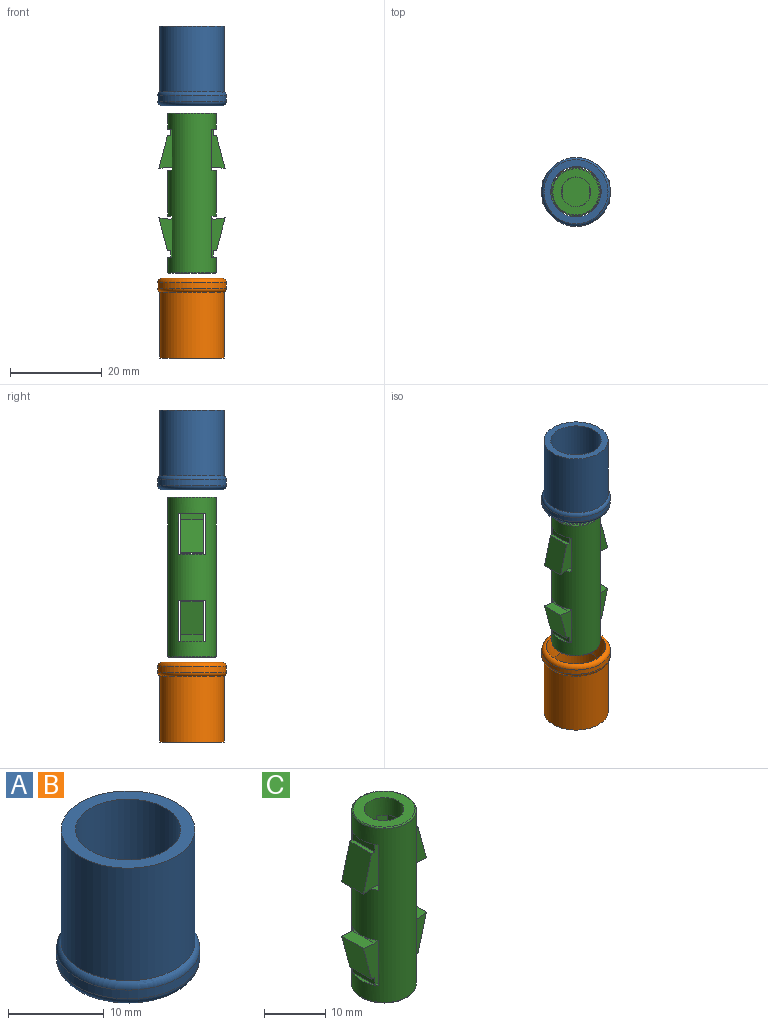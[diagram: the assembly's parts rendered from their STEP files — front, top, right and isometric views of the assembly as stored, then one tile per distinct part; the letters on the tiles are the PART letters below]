
ASSEMBLY  parts=3 mates=2
PART A: 7 faces, bbox 16.2x16.2x17.4 mm
  f0: cylinder r=7mm len=14.4mm, axis (0,0,-1), area 633.3mm2, adj f2,f5
  f1: cylinder r=5.5mm len=12.4mm, axis (0,0,-1), area 428.5mm2, adj f2,f6
  f2: plane 14x14mm, normal (0,0,1), area 58.9mm2, adj f0,f1
  f3: cylinder r=7.5mm len=15mm, axis (0,0,-1), area 53.4mm2, adj f4,f5
  f4: torus R=6.5mm, axis (0,0,1), area 70.4mm2, adj f3,f6
  f5: torus R=6.5mm, axis (0,0,1), area 48.2mm2, adj f0,f3
  f6: cone r=6.5mm half-angle=11.3deg, axis (0,0,-1), area 192.2mm2, adj f1,f4
PART B: same geometry as A
PART C: 89 faces, bbox 14.5x11.4x35 mm
  f0: cylinder r=3.25mm len=17mm, axis (0,0,-1), area 209.6mm2, adj f1,f2,f4,f12,f13,f14,f15,f17
  f1: plane 3.37x3mm, normal (0,0,1), area 2.3mm2, adj f0,f10,f13,f77,f83
  f2: plane 3.37x3mm, normal (0,0,1), area 2.3mm2, adj f0,f10,f15,f77,f84
  f3: plane 4.87x0.6mm, normal (0,0,1), area 2mm2, adj f10,f66
  f4: plane 3.37x3mm, normal (0,0,1), area 2.3mm2, adj f0,f10,f18,f64,f70
  f5: plane 4.87x0.6mm, normal (0,0,-1), area 2mm2, adj f10,f52
  f6: plane 3.37x3mm, normal (0,0,-1), area 2.3mm2, adj f9,f10,f26,f51,f55
  f7: plane 3.37x3mm, normal (0,0,-1), area 2.3mm2, adj f9,f10,f21,f35,f42
  f8: plane 4.87x0.6mm, normal (0,0,-1), area 2mm2, adj f10,f33
  f9: cylinder r=3.25mm len=17mm, axis (0,0,-1), area 209.6mm2, adj f6,f7,f11,f21,f22,f23,f24,f25
  f10: cylinder r=5.25mm len=34.6mm, axis (0,0,-1), area 911.4mm2, adj f1,f2,f3,f4,f5,f6,f7,f8
  f11: plane 10.1x10.1mm, normal (0,0,1), area 46.9mm2, adj f9,f88
  f12: plane 10.1x10.1mm, normal (0,0,-1), area 46.9mm2, adj f0,f87
  f13: plane 9x3.06mm, normal (0,1,0), area 27.5mm2, adj f0,f1,f10,f14
  f14: plane 6x4mm, normal (0,0,-1), area 13.5mm2, adj f0,f10,f13,f15
  f15: plane 9x3.06mm, normal (0,-1,0), area 27.5mm2, adj f0,f2,f10,f14
  f16: plane 4.87x0.6mm, normal (0,0,1), area 2mm2, adj f10,f76
  f17: plane 3.37x3mm, normal (0,0,1), area 2.3mm2, adj f0,f10,f20,f64,f69
  f18: plane 9x3.06mm, normal (0,-1,0), area 27.5mm2, adj f0,f4,f10,f19
  f19: plane 6x4mm, normal (0,0,-1), area 13.5mm2, adj f0,f10,f18,f20
  f20: plane 9x3.06mm, normal (0,1,0), area 27.5mm2, adj f0,f10,f17,f19
  f21: plane 9x3.06mm, normal (0,-1,0), area 27.5mm2, adj f7,f9,f10,f22
  f22: plane 6x4mm, normal (0,0,1), area 13.5mm2, adj f9,f10,f21,f23
  f23: plane 9x3.06mm, normal (0,1,0), area 27.5mm2, adj f9,f10,f22,f24
  f24: plane 3.37x3mm, normal (0,0,-1), area 2.3mm2, adj f9,f10,f23,f35,f41
  f25: plane 3.37x3mm, normal (0,0,-1), area 2.3mm2, adj f9,f10,f28,f51,f56
  f26: plane 9x3.06mm, normal (0,1,0), area 27.5mm2, adj f6,f9,f10,f27
  f27: plane 6x4mm, normal (0,0,1), area 13.5mm2, adj f9,f10,f26,f28
  f28: plane 9x3.06mm, normal (0,-1,0), area 27.5mm2, adj f9,f10,f25,f27
  f29: plane 0.06x0.03mm, normal (0,0,1), area 0mm2, adj f10,f33,f42
  f30: plane 5x2.58mm, normal (-0.12,0,-0.99), area 13mm2, adj f31,f40,f41,f42
  f31: plane 7.1x5mm, normal (0.97,0,0.26), area 36.7mm2, adj f30,f32,f41,f42
  f32: plane 5x0.7mm, normal (0,0,1), area 3.5mm2, adj f31,f33,f41,f42
  f33: plane 5x1.5mm, normal (1,0,0), area 7.5mm2, adj f8,f29,f32,f34,f41,f42
  f34: plane 0.06x0.03mm, normal (0,0,1), area 0mm2, adj f10,f33,f41
  f35: plane 7.8x5mm, normal (-1,0,0), area 39mm2, adj f7,f24,f36,f41,f42
  f36: plane 5x0.25mm, normal (0,0,1), area 1.2mm2, adj f35,f37,f41,f42
  f37: plane 5x0.5mm, normal (-1,0,0), area 2.5mm2, adj f36,f38,f41,f42
  f38: plane 5x0.25mm, normal (0,0,-1), area 1.2mm2, adj f37,f39,f41,f42
  f39: plane 5x0.5mm, normal (-1,0,0), area 2.5mm2, adj f38,f40,f41,f42
  f40: plane 5x1.41mm, normal (0.34,0,-0.94), area 7.5mm2, adj f30,f39,f41,f42
  f41: plane 8.8x4.25mm, normal (0,-1,0), area 23.4mm2, adj f24,f30,f31,f32,f33,f34,f35,f36
  f42: plane 8.8x4.25mm, normal (0,1,0), area 23.4mm2, adj f7,f29,f30,f31,f32,f33,f35,f36
  f43: plane 0.06x0.03mm, normal (0,0,1), area 0mm2, adj f10,f52,f55
  f44: plane 0.06x0.03mm, normal (0,0,1), area 0mm2, adj f10,f52,f56
  f45: plane 5x2.58mm, normal (0.12,0,-0.99), area 13mm2, adj f46,f54,f55,f56
  f46: plane 5x1.41mm, normal (-0.34,0,-0.94), area 7.5mm2, adj f45,f47,f55,f56
  f47: plane 5x0.5mm, normal (1,0,0), area 2.5mm2, adj f46,f48,f55,f56
  f48: plane 5x0.25mm, normal (0,0,-1), area 1.2mm2, adj f47,f49,f55,f56
  f49: plane 5x0.5mm, normal (1,0,0), area 2.5mm2, adj f48,f50,f55,f56
  f50: plane 5x0.25mm, normal (0,0,1), area 1.2mm2, adj f49,f51,f55,f56
  f51: plane 7.8x5mm, normal (1,0,0), area 39mm2, adj f6,f25,f50,f55,f56
  f52: plane 5x1.5mm, normal (-1,0,0), area 7.5mm2, adj f5,f43,f44,f53,f55,f56
  f53: plane 5x0.7mm, normal (0,0,1), area 3.5mm2, adj f52,f54,f55,f56
  f54: plane 7.1x5mm, normal (-0.97,0,0.26), area 36.7mm2, adj f45,f53,f55,f56
  f55: plane 8.8x4.25mm, normal (0,-1,0), area 23.4mm2, adj f6,f43,f45,f46,f47,f48,f49,f50
  f56: plane 8.8x4.25mm, normal (0,1,0), area 23.4mm2, adj f25,f44,f45,f46,f47,f48,f49,f50
  f57: plane 0.06x0.03mm, normal (0,0,-1), area 0mm2, adj f10,f66,f70
  f58: plane 5x2.58mm, normal (-0.12,0,0.99), area 13mm2, adj f59,f68,f69,f70
  f59: plane 5x1.41mm, normal (0.34,0,0.94), area 7.5mm2, adj f58,f60,f69,f70
  f60: plane 5x0.5mm, normal (-1,0,0), area 2.5mm2, adj f59,f61,f69,f70
  f61: plane 5x0.25mm, normal (0,0,1), area 1.2mm2, adj f60,f62,f69,f70
  f62: plane 5x0.5mm, normal (-1,0,0), area 2.5mm2, adj f61,f63,f69,f70
  f63: plane 5x0.25mm, normal (0,0,-1), area 1.2mm2, adj f62,f64,f69,f70
  f64: plane 7.8x5mm, normal (-1,0,0), area 39mm2, adj f4,f17,f63,f69,f70
  f65: plane 0.06x0.03mm, normal (0,0,-1), area 0mm2, adj f10,f66,f69
  f66: plane 5x1.5mm, normal (1,0,0), area 7.5mm2, adj f3,f57,f65,f67,f69,f70
  f67: plane 5x0.7mm, normal (0,0,-1), area 3.5mm2, adj f66,f68,f69,f70
  f68: plane 7.1x5mm, normal (0.97,0,-0.26), area 36.7mm2, adj f58,f67,f69,f70
  f69: plane 8.8x4.25mm, normal (0,-1,0), area 23.4mm2, adj f17,f58,f59,f60,f61,f62,f63,f64
  f70: plane 8.8x4.25mm, normal (0,1,0), area 23.4mm2, adj f4,f57,f58,f59,f60,f61,f62,f63
  f71: plane 0.06x0.03mm, normal (0,0,-1), area 0mm2, adj f10,f76,f83
  f72: plane 0.06x0.03mm, normal (0,0,-1), area 0mm2, adj f10,f76,f84
  f73: plane 5x2.58mm, normal (0.12,0,0.99), area 13mm2, adj f74,f82,f83,f84
  f74: plane 7.1x5mm, normal (-0.97,0,-0.26), area 36.7mm2, adj f73,f75,f83,f84
  f75: plane 5x0.7mm, normal (0,0,-1), area 3.5mm2, adj f74,f76,f83,f84
  f76: plane 5x1.5mm, normal (-1,0,0), area 7.5mm2, adj f16,f71,f72,f75,f83,f84
  f77: plane 7.8x5mm, normal (1,0,0), area 39mm2, adj f1,f2,f78,f83,f84
  f78: plane 5x0.25mm, normal (0,0,-1), area 1.2mm2, adj f77,f79,f83,f84
  f79: plane 5x0.5mm, normal (1,0,0), area 2.5mm2, adj f78,f80,f83,f84
  f80: plane 5x0.25mm, normal (0,0,1), area 1.2mm2, adj f79,f81,f83,f84
  f81: plane 5x0.5mm, normal (1,0,0), area 2.5mm2, adj f80,f82,f83,f84
  f82: plane 5x1.41mm, normal (-0.34,0,0.94), area 7.5mm2, adj f73,f81,f83,f84
  f83: plane 8.8x4.25mm, normal (0,-1,0), area 23.4mm2, adj f1,f71,f73,f74,f75,f76,f77,f78
  f84: plane 8.8x4.25mm, normal (0,1,0), area 23.4mm2, adj f2,f72,f73,f74,f75,f76,f77,f78
  f85: plane 6.5x6.5mm, normal (0,0,-1), area 33.2mm2, adj f0
  f86: plane 6.5x6.5mm, normal (0,0,1), area 33.2mm2, adj f9
  f87: torus R=5.05mm, axis (0,0,1), area 10.2mm2, adj f10,f12
  f88: torus R=5.05mm, axis (0,0,1), area 10.2mm2, adj f10,f11
PLACE A t=(-2.54,4.35,-1.15)mm
PLACE B rot(axis=(-1,0,0),180deg) t=(-2.54,4.35,-38.86)mm
PLACE C t=(-2.54,4.35,-20.25)mm
MATE slider A.f1 <-> C.f10  axis (0,0,-1) through (-2.54,4.35,3.85)mm
MATE slider C.f10 <-> B.f1  axis (0,0,-1) through (-2.54,4.35,-20.25)mm
